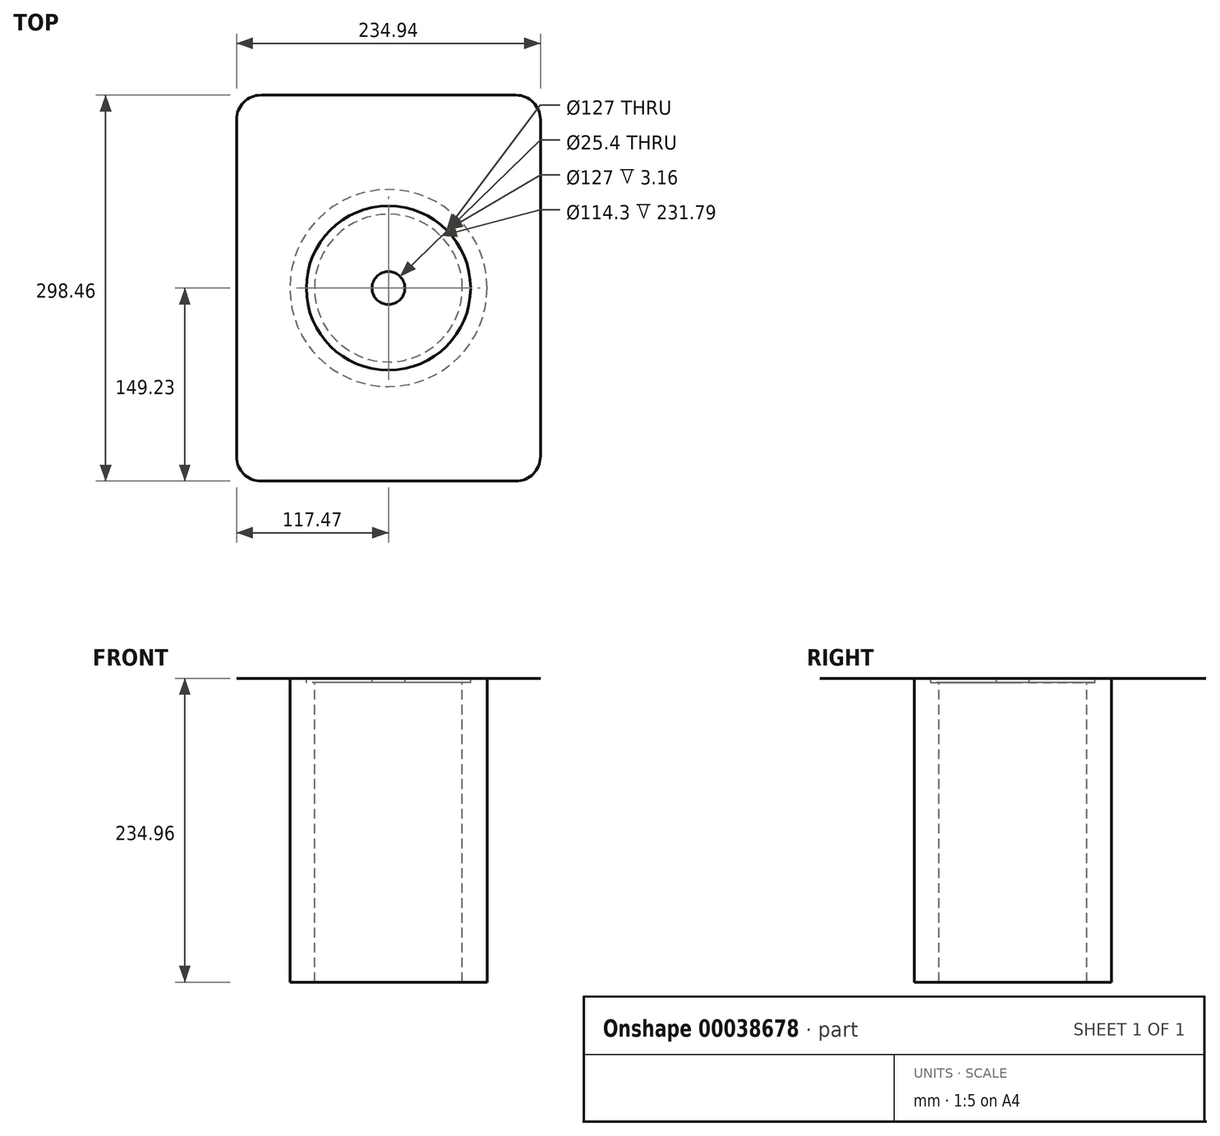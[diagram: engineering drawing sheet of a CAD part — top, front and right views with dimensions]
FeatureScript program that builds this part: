
annotation { "Feature Type Name" : "Feature", "Feature Type Description" : "" }
export const myFeature = defineFeature(function(context is Context, id is Id, definition is map)
    precondition{}
    {
        {
            var Q0;
            Q0=qCreatedBy(makeId("Top.planeOp"),FACE);
            var sketch = newSketch(context, id + "F0", { "sketchPlane" : qUnion([Q0])});
            skCircle(sketch, "E0", {"center": v(0, 0) * mm, "radius": 76.2 * mm});
            skSolve(sketch);
        }
        {
            var Q0;
            Q0=makeQuery(id+"F0.imprint","IMPRINT",FACE,{"disambiguationData":[TD([[makeQuery(id+"F0.imprint","IMPRINT",EDGE,{"derivedFrom":sQuery(id+"F0.wireOp",EDGE,"E0")}),1.0]])]});
            extrude(context, id + "F1", {"entities" : qUnion([Q0]), "depth" : 234.95 * mm});
        }
        {
            var Q0;
            Q0=makeQuery(id+"F1.opExtrude","CAP_FACE",FACE,{"disambiguationData":[OSD([sQuery(id+"F0.wireOp",EDGE,"E0")])],"isStart":false});
            var sketch = newSketch(context, id + "F2", { "sketchPlane" : qUnion([Q0])});
            skLineSegment(sketch, "E1.rect.bottom", {"start": v(117.48, 149.23) * mm, "end": v(-117.47, 149.23) * mm});
            skLineSegment(sketch, "E1.rect.top", {"start": v(117.47, -149.23) * mm, "end": v(-117.48, -149.23) * mm});
            skLineSegment(sketch, "E1.rect.left", {"start": v(117.48, 149.23) * mm, "end": v(117.48, -149.23) * mm});
            skLineSegment(sketch, "E1.rect.right", {"start": v(-117.48, 149.23) * mm, "end": v(-117.48, -149.23) * mm});
            skPoint(sketch, "E1.rect.middle", {"position": v(0, 0) * mm});
            skSolve(sketch);
        }
        {
            var Q0;
            Q0=makeQuery(id+"F2.imprint","IMPRINT",FACE,{"disambiguationData":[TD([[makeQuery(id+"F2.imprint","IMPRINT",EDGE,{"derivedFrom":makeQuery(id+"F1.opExtrude","CAP_EDGE",EDGE,{"disambiguationData":[OSD([sQuery(id+"F0.wireOp",EDGE,"E0")])],"isStart":false})}),1.0]])]});
            var Q1;
            Q1=makeQuery(id+"F2.imprint","IMPRINT",FACE,{"disambiguationData":[TD([[makeQuery(id+"F2.imprint","IMPRINT",EDGE,{"derivedFrom":sQuery(id+"F2.wireOp",EDGE,"E1.rect.bottom")}),1.0]])]});
            extrude(context, id + "F3", {"entities" : qUnion([Q0, Q1]), "depth" : 3 / 203.2 * mm});
        }
        {
            var Q0;
            Q0=makeQuery(id+"F3.opExtrude","SWEPT_EDGE",EDGE,{"disambiguationData":[OSD([sQuery(id+"F2.wireOp",EDGE,"E1.rect.top"),sQuery(id+"F2.wireOp",EDGE,"E1.rect.left")])]});
            var Q1;
            Q1=makeQuery(id+"F3.opExtrude","SWEPT_EDGE",EDGE,{"disambiguationData":[OSD([sQuery(id+"F2.wireOp",EDGE,"E1.rect.top"),sQuery(id+"F2.wireOp",EDGE,"E1.rect.right")])]});
            var Q2;
            Q2=makeQuery(id+"F3.opExtrude","SWEPT_EDGE",EDGE,{"disambiguationData":[OSD([sQuery(id+"F2.wireOp",EDGE,"E1.rect.bottom"),sQuery(id+"F2.wireOp",EDGE,"E1.rect.left")])]});
            var Q3;
            Q3=makeQuery(id+"F3.opExtrude","SWEPT_EDGE",EDGE,{"disambiguationData":[OSD([sQuery(id+"F2.wireOp",EDGE,"E1.rect.bottom"),sQuery(id+"F2.wireOp",EDGE,"E1.rect.right")])]});
            fillet(context, id + "F4", {"entities" : qUnion([Q0, Q1, Q2, Q3]), "radius" : 19.05 * mm, "tangentPropagation" : true, "allowEdgeOverflow" : false});
        }
        {
            var Q0;
            Q0=makeQuery(id+"F3.opExtrude","CAP_FACE",FACE,{"disambiguationData":[OSD([sQuery(id+"F2.wireOp",EDGE,"E1.rect.bottom"),sQuery(id+"F2.wireOp",EDGE,"E1.rect.top"),sQuery(id+"F2.wireOp",EDGE,"E1.rect.left"),sQuery(id+"F2.wireOp",EDGE,"E1.rect.right")])],"isStart":false});
            var sketch = newSketch(context, id + "F5", { "sketchPlane" : qUnion([Q0])});
            skLineSegment(sketch, "E2", {"start": v(-117.48, 0) * mm, "end": v(117.48, 0) * mm});
            skCircle(sketch, "E3", {"center": v(0, 0) * mm, "radius": 63.5 * mm});
            skSolve(sketch);
        }
        {
            var Q0;
            {var subQ0=sQuery(id+"F5.wireOp",EDGE,"E3");var subQ1=sQuery(id+"F5.wireOp",EDGE,"E2");var subQ3=makeQuery(id+"F5.imprint","INTERSECT",VERTEX,{"disambiguationData":[OD(0.0)],"derivedFrom":[subQ1,subQ0]});Q0=makeQuery(id+"F5.imprint","IMPRINT",FACE,{"disambiguationData":[TD([[makeQuery(id+"F5.imprint","IMPRINT",EDGE,{"disambiguationData":[TD([[subQ3,-1.0]])],"derivedFrom":subQ1}),-1.0]])]});}
            var Q1;
            {var subQ0=sQuery(id+"F5.wireOp",EDGE,"E3");var subQ1=sQuery(id+"F5.wireOp",EDGE,"E2");var subQ3=makeQuery(id+"F5.imprint","INTERSECT",VERTEX,{"disambiguationData":[OD(0.0)],"derivedFrom":[subQ1,subQ0]});Q1=makeQuery(id+"F5.imprint","IMPRINT",FACE,{"disambiguationData":[TD([[makeQuery(id+"F5.imprint","IMPRINT",EDGE,{"disambiguationData":[TD([[subQ3,-1.0]])],"derivedFrom":subQ1}),1.0]])]});}
            extrude(context, id + "F6", {"entities" : qUnion([Q0, Q1]), "operationType" : NewBodyOperationType.REMOVE, "oppositeDirection" : true, "depth" : 3.17 * mm});
        }
        {
            var Q0;
            Q0=makeQuery(id+"F6.boolean.opBoolean","COPY",FACE,{"derivedFrom":makeQuery(id+"F6.opExtrude","CAP_FACE",FACE,{"disambiguationData":[OSD([sQuery(id+"F5.wireOp",EDGE,"E3")])],"isStart":false})});
            var sketch = newSketch(context, id + "F7", { "sketchPlane" : qUnion([Q0])});
            skCircle(sketch, "E4.0", {"center": v(0, 0) * mm, "radius": 57.15 * mm});
            skSolve(sketch);
        }
        {
            var Q0;
            Q0 = qSketchRegion(id + "F7", true);
            extrude(context, id + "F8", {"entities" : qUnion([Q0]), "operationType" : NewBodyOperationType.REMOVE, "endBound" : BoundingType.THROUGH_ALL, "oppositeDirection" : true, "depth" : 25.4 * mm});
        }
        {
            var Q0;
            Q0=makeQuery(id+"F3.opExtrude","CAP_FACE",FACE,{"disambiguationData":[OSD([sQuery(id+"F2.wireOp",EDGE,"E1.rect.bottom"),sQuery(id+"F2.wireOp",EDGE,"E1.rect.top"),sQuery(id+"F2.wireOp",EDGE,"E1.rect.left"),sQuery(id+"F2.wireOp",EDGE,"E1.rect.right")])],"isStart":false});
            var sketch = newSketch(context, id + "F9", { "sketchPlane" : qUnion([Q0])});
            skCircle(sketch, "E5.0", {"center": v(0, 0) * mm, "radius": 63.5 * mm});
            skCircle(sketch, "E6", {"center": v(0, 0) * mm, "radius": 12.7 * mm});
            skSolve(sketch);
        }
        {
            var Q0;
            Q0 = qSketchRegion(id + "F9", true);
            var Q1;
            Q1=makeQuery(id+"F6.boolean.opBoolean","COPY",FACE,{"derivedFrom":makeQuery(id+"F6.opExtrude","CAP_FACE",FACE,{"disambiguationData":[OSD([sQuery(id+"F5.wireOp",EDGE,"E3")])],"isStart":false})});
            extrude(context, id + "F10", {"entities" : qUnion([Q0]), "endBound" : BoundingType.UP_TO_SURFACE, "oppositeDirection" : true, "endBoundEntityFace" : qUnion([Q1]), "depth" : 25.4 * mm});
        }
    });
